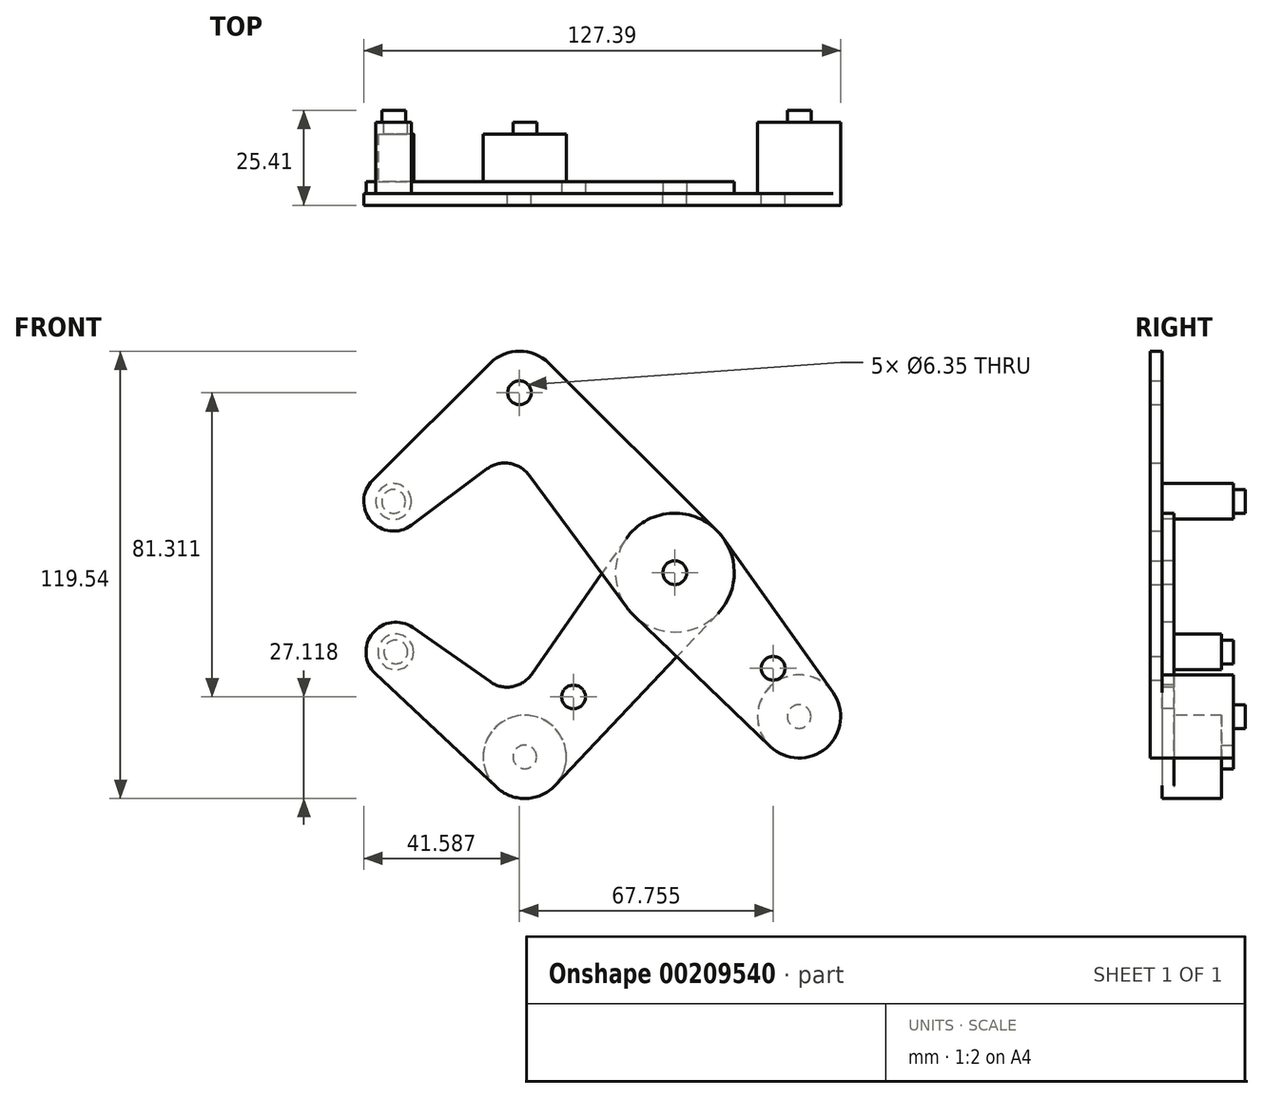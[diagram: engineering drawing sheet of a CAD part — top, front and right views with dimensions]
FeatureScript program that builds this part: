
annotation { "Feature Type Name" : "Feature", "Feature Type Description" : "" }
export const myFeature = defineFeature(function(context is Context, id is Id, definition is map)
    precondition{}
    {
        {
            var Q0;
            Q0=qCreatedBy(makeId("Front.planeOp"),FACE);
            var sketch = newSketch(context, id + "F0", { "sketchPlane" : qUnion([Q0])});
            skLineSegment(sketch, "E0", {"start": v(-41.5, 48.07) * mm, "end": v(41.5, -48.07) * mm, "construction": true});
            skCircle(sketch, "E1", {"center": v(0, 0) * mm, "radius": 3.18 * mm});
            skCircle(sketch, "E2", {"center": v(33.2, -38.45) * mm, "radius": 3.18 * mm});
            skCircle(sketch, "E3", {"center": v(-41.5, 48.07) * mm, "radius": 3.18 * mm});
            skCircle(sketch, "E4", {"center": v(-75.14, 19.02) * mm, "radius": 3.18 * mm});
            skLineSegment(sketch, "E5", {"start": v(-41.5, 48.07) * mm, "end": v(-75.14, 19.02) * mm, "construction": true});
            skCircle(sketch, "E6", {"center": v(33.2, -38.45) * mm, "radius": 11.11 * mm});
            skCircle(sketch, "E7", {"center": v(-75.14, 19.02) * mm, "radius": 7.94 * mm});
            skCircle(sketch, "E8", {"center": v(-41.5, 48.07) * mm, "radius": 11.11 * mm});
            skLineSegment(sketch, "E9", {"start": v(-80.74, 24.65) * mm, "end": v(-49.34, 55.94) * mm});
            skLineSegment(sketch, "E10", {"start": v(-70.4, 12.66) * mm, "end": v(-50.18, 27.73) * mm});
            skCircle(sketch, "E11", {"center": v(0, 0) * mm, "radius": 15.88 * mm});
            skLineSegment(sketch, "E12", {"start": v(-33.65, 55.94) * mm, "end": v(11.2, 11.25) * mm});
            skLineSegment(sketch, "E13", {"start": v(-39.05, 26.09) * mm, "end": v(-12.76, -9.44) * mm});
            skLineSegment(sketch, "E14", {"start": v(-11, -11.45) * mm, "end": v(25.5, -46.47) * mm});
            skLineSegment(sketch, "E15", {"start": v(12.94, 9.2) * mm, "end": v(42.25, -32.01) * mm});
            skArc(sketch, "E16.filletArc", {"start": v(-39.05, 26.09) * mm, "mid": v(-44.28, 29.22) * mm, "end": v(-50.18, 27.73) * mm});
            skLineSegment(sketch, "E17", {"start": v(0, 0) * mm, "end": v(-40.09, -49.25) * mm, "construction": true});
            skLineSegment(sketch, "E18", {"start": v(-40.09, -49.25) * mm, "end": v(-74.56, -21.19) * mm, "construction": true});
            skCircle(sketch, "E19", {"center": v(-74.56, -21.19) * mm, "radius": 3.18 * mm});
            skCircle(sketch, "E20", {"center": v(-40.09, -49.25) * mm, "radius": 3.18 * mm});
            skCircle(sketch, "E21", {"center": v(-74.56, -21.19) * mm, "radius": 7.94 * mm});
            skCircle(sketch, "E22", {"center": v(-40.09, -49.25) * mm, "radius": 11.11 * mm});
            skLineSegment(sketch, "E23", {"start": v(-70, -14.69) * mm, "end": v(-49.36, -29.17) * mm});
            skLineSegment(sketch, "E24", {"start": v(-80, -26.97) * mm, "end": v(-47.7, -57.34) * mm});
            skLineSegment(sketch, "E25", {"start": v(-13.03, 9.07) * mm, "end": v(-38.28, -27.2) * mm});
            skLineSegment(sketch, "E26", {"start": v(11.53, -10.92) * mm, "end": v(-32.02, -56.89) * mm});
            skArc(sketch, "E27.filletArc", {"start": v(-49.36, -29.17) * mm, "mid": v(-43.41, -30.49) * mm, "end": v(-38.28, -27.2) * mm});
            skCircle(sketch, "E28", {"center": v(-27.06, -33.24) * mm, "radius": 3.18 * mm});
            skCircle(sketch, "E29", {"center": v(26.26, -25.56) * mm, "radius": 3.18 * mm});
            skLineSegment(sketch, "E30", {"start": v(26.26, -25.56) * mm, "end": v(23.86, -27.64) * mm, "construction": true});
            skCircle(sketch, "E31", {"center": v(0, 0) * mm, "radius": 3.97 * mm});
            skSolve(sketch);
        }
        {
            var Q0;
            Q0=qCreatedBy(makeId("Front.planeOp"),FACE);
            cPlane(context, id + "F1", {"entities" : qUnion([Q0]), "cplaneType" : CPlaneType.OFFSET, "offset" : 9.52 * mm, "oppositeDirection" : true, "width" : 254 * mm, "height" : 254 * mm});
        }
        {
            var Q0;
            Q0=makeQuery(id+"F0.imprint","IMPRINT",FACE,{"disambiguationData":[TD([[makeQuery(id+"F0.imprint","IMPRINT",EDGE,{"derivedFrom":sQuery(id+"F0.wireOp",EDGE,"E4")}),-1.0]])]});
            var Q1;
            {var subQ1=sQuery(id+"F0.wireOp",EDGE,"E9");Q1=makeQuery(id+"F0.imprint","IMPRINT",FACE,{"disambiguationData":[TD([[makeQuery(id+"F0.imprint","IMPRINT",EDGE,{"derivedFrom":subQ1}),-1.0]])]});}
            var Q2;
            Q2=makeQuery(id+"F0.imprint","IMPRINT",FACE,{"disambiguationData":[TD([[makeQuery(id+"F0.imprint","IMPRINT",EDGE,{"derivedFrom":sQuery(id+"F0.wireOp",EDGE,"E3")}),-1.0]])]});
            var Q3;
            {var subQ0=sQuery(id+"F0.wireOp",EDGE,"E13");var subQ1=sQuery(id+"F0.wireOp",EDGE,"E11");var subQ2=makeQuery(id+"F0.imprint","INTERSECT",VERTEX,{"derivedFrom":[subQ1,subQ0]});Q3=makeQuery(id+"F0.imprint","IMPRINT",FACE,{"disambiguationData":[TD([[makeQuery(id+"F0.imprint","IMPRINT",EDGE,{"disambiguationData":[TD([[subQ2,1.0]])],"derivedFrom":subQ1}),-1.0]])]});}
            var Q4;
            Q4=makeQuery(id+"F0.imprint","IMPRINT",FACE,{"disambiguationData":[TD([[makeQuery(id+"F0.imprint","IMPRINT",EDGE,{"derivedFrom":sQuery(id+"F0.wireOp",EDGE,"E31")}),-1.0]])]});
            var Q5;
            {var subQ0=sQuery(id+"F0.wireOp",EDGE,"E14");var subQ1=sQuery(id+"F0.wireOp",EDGE,"E11");var subQ2=makeQuery(id+"F0.imprint","INTERSECT",VERTEX,{"derivedFrom":[subQ1,subQ0]});Q5=makeQuery(id+"F0.imprint","IMPRINT",FACE,{"disambiguationData":[TD([[makeQuery(id+"F0.imprint","IMPRINT",EDGE,{"disambiguationData":[TD([[subQ2,-1.0]])],"derivedFrom":subQ1}),-1.0]])]});}
            var Q6;
            Q6=makeQuery(id+"F0.imprint","IMPRINT",FACE,{"disambiguationData":[TD([[makeQuery(id+"F0.imprint","IMPRINT",EDGE,{"derivedFrom":sQuery(id+"F0.wireOp",EDGE,"E1")}),-1.0]])]});
            var Q7;
            {var subQ0=sQuery(id+"F0.wireOp",EDGE,"E15");Q7=makeQuery(id+"F0.imprint","IMPRINT",FACE,{"disambiguationData":[TD([[makeQuery(id+"F0.imprint","IMPRINT",EDGE,{"derivedFrom":subQ0}),-1.0]])]});}
            var Q8;
            Q8=makeQuery(id+"F0.imprint","IMPRINT",FACE,{"disambiguationData":[TD([[makeQuery(id+"F0.imprint","IMPRINT",EDGE,{"derivedFrom":sQuery(id+"F0.wireOp",EDGE,"E2")}),-1.0]])]});
            extrude(context, id + "F2", {"entities" : qUnion([Q0, Q1, Q2, Q3, Q4, Q5, Q6, Q7, Q8]), "depth" : 3.17 * mm});
        }
        {
            var Q0;
            Q0=makeQuery(id+"F0.imprint","IMPRINT",FACE,{"disambiguationData":[TD([[makeQuery(id+"F0.imprint","IMPRINT",EDGE,{"derivedFrom":sQuery(id+"F0.wireOp",EDGE,"E19")}),-1.0]])]});
            var Q1;
            {var subQ10=sQuery(id+"F0.wireOp",EDGE,"E23");Q1=makeQuery(id+"F0.imprint","IMPRINT",FACE,{"disambiguationData":[TD([[makeQuery(id+"F0.imprint","IMPRINT",EDGE,{"derivedFrom":subQ10}),-1.0]])]});}
            var Q2;
            Q2=makeQuery(id+"F0.imprint","IMPRINT",FACE,{"disambiguationData":[TD([[makeQuery(id+"F0.imprint","IMPRINT",EDGE,{"derivedFrom":sQuery(id+"F0.wireOp",EDGE,"E20")}),-1.0]])]});
            var Q3;
            {var subQ0=sQuery(id+"F0.wireOp",EDGE,"E13");var subQ1=sQuery(id+"F0.wireOp",EDGE,"E11");var subQ2=makeQuery(id+"F0.imprint","INTERSECT",VERTEX,{"derivedFrom":[subQ1,subQ0]});Q3=makeQuery(id+"F0.imprint","IMPRINT",FACE,{"disambiguationData":[TD([[makeQuery(id+"F0.imprint","IMPRINT",EDGE,{"disambiguationData":[TD([[subQ2,1.0]])],"derivedFrom":subQ1}),-1.0]])]});}
            var Q4;
            {var subQ0=sQuery(id+"F0.wireOp",EDGE,"E14");var subQ1=sQuery(id+"F0.wireOp",EDGE,"E11");var subQ2=makeQuery(id+"F0.imprint","INTERSECT",VERTEX,{"derivedFrom":[subQ1,subQ0]});Q4=makeQuery(id+"F0.imprint","IMPRINT",FACE,{"disambiguationData":[TD([[makeQuery(id+"F0.imprint","IMPRINT",EDGE,{"disambiguationData":[TD([[subQ2,-1.0]])],"derivedFrom":subQ1}),-1.0]])]});}
            var Q5;
            Q5=makeQuery(id+"F0.imprint","IMPRINT",FACE,{"disambiguationData":[TD([[makeQuery(id+"F0.imprint","IMPRINT",EDGE,{"derivedFrom":sQuery(id+"F0.wireOp",EDGE,"E31")}),-1.0]])]});
            var Q6;
            Q6=makeQuery(id+"F0.imprint","IMPRINT",FACE,{"disambiguationData":[TD([[makeQuery(id+"F0.imprint","IMPRINT",EDGE,{"derivedFrom":sQuery(id+"F0.wireOp",EDGE,"E1")}),-1.0]])]});
            extrude(context, id + "F3", {"entities" : qUnion([Q0, Q1, Q2, Q3, Q4, Q5, Q6]), "oppositeDirection" : true, "depth" : 3.17 * mm});
        }
        {
            var Q0;
            Q0=makeQuery(id+"F2.opExtrude","CAP_FACE",FACE,{"disambiguationData":[OSD([sQuery(id+"F0.wireOp",EDGE,"E1"),sQuery(id+"F0.wireOp",EDGE,"E2"),sQuery(id+"F0.wireOp",EDGE,"E3"),sQuery(id+"F0.wireOp",EDGE,"E4"),sQuery(id+"F0.wireOp",EDGE,"E6"),sQuery(id+"F0.wireOp",EDGE,"E7"),sQuery(id+"F0.wireOp",EDGE,"E8"),sQuery(id+"F0.wireOp",EDGE,"E9"),sQuery(id+"F0.wireOp",EDGE,"E10"),sQuery(id+"F0.wireOp",EDGE,"E11"),sQuery(id+"F0.wireOp",EDGE,"E12"),sQuery(id+"F0.wireOp",EDGE,"E13"),sQuery(id+"F0.wireOp",EDGE,"E14"),sQuery(id+"F0.wireOp",EDGE,"E15"),sQuery(id+"F0.wireOp",EDGE,"E16.filletArc"),sQuery(id+"F0.wireOp",EDGE,"E29")])],"isStart":false});
            var sketch = newSketch(context, id + "F4", { "sketchPlane" : qUnion([Q0])});
            skCircle(sketch, "E32", {"center": v(-75.14, 19.02) * mm, "radius": 4.76 * mm});
            skCircle(sketch, "E33", {"center": v(33.2, -38.45) * mm, "radius": 11.11 * mm});
            skSolve(sketch);
        }
        {
            var Q0;
            {var subQ10=sQuery(id+"F0.wireOp",EDGE,"E23");Q0=makeQuery(id+"F0.imprint","IMPRINT",FACE,{"disambiguationData":[TD([[makeQuery(id+"F0.imprint","IMPRINT",EDGE,{"derivedFrom":subQ10}),-1.0]])]});}
            var sketch = newSketch(context, id + "F5", { "sketchPlane" : qUnion([Q0])});
            skCircle(sketch, "E34", {"center": v(-74.56, -21.19) * mm, "radius": 4.76 * mm});
            skCircle(sketch, "E35", {"center": v(-40.09, -49.25) * mm, "radius": 11.11 * mm});
            skSolve(sketch);
        }
        {
            var Q0;
            Q0=qSketchRegion(id+"F5",true);
            var Q1;
            Q1=qSketchRegion(id+"F4",true);
            var Q2;
            Q2=qCreatedBy(id+"F1.planeOp",FACE);
            extrude(context, id + "F6", {"entities" : qUnion([Q0, Q1]), "endBound" : BoundingType.UP_TO_SURFACE, "oppositeDirection" : true, "endBoundEntityFace" : qUnion([Q2]), "depth" : 25.4 * mm});
        }
        {
            var Q0;
            Q0=makeQuery(id+"F2.opExtrude","SWEPT_BODY",BODY,{"disambiguationData":[OSD([sQuery(id+"F0.wireOp",EDGE,"E1"),sQuery(id+"F0.wireOp",EDGE,"E2"),sQuery(id+"F0.wireOp",EDGE,"E3"),sQuery(id+"F0.wireOp",EDGE,"E4"),sQuery(id+"F0.wireOp",EDGE,"E6"),sQuery(id+"F0.wireOp",EDGE,"E7"),sQuery(id+"F0.wireOp",EDGE,"E8"),sQuery(id+"F0.wireOp",EDGE,"E9"),sQuery(id+"F0.wireOp",EDGE,"E10"),sQuery(id+"F0.wireOp",EDGE,"E11"),sQuery(id+"F0.wireOp",EDGE,"E12"),sQuery(id+"F0.wireOp",EDGE,"E13"),sQuery(id+"F0.wireOp",EDGE,"E14"),sQuery(id+"F0.wireOp",EDGE,"E15"),sQuery(id+"F0.wireOp",EDGE,"E16.filletArc"),sQuery(id+"F0.wireOp",EDGE,"E29")])]});
            var Q1;
            Q1=makeQuery(id+"F3.opExtrude","SWEPT_BODY",BODY,{"disambiguationData":[OSD([sQuery(id+"F0.wireOp",EDGE,"E1"),sQuery(id+"F0.wireOp",EDGE,"E11"),sQuery(id+"F0.wireOp",EDGE,"E19"),sQuery(id+"F0.wireOp",EDGE,"E20"),sQuery(id+"F0.wireOp",EDGE,"E21"),sQuery(id+"F0.wireOp",EDGE,"E22"),sQuery(id+"F0.wireOp",EDGE,"E23"),sQuery(id+"F0.wireOp",EDGE,"E24"),sQuery(id+"F0.wireOp",EDGE,"E25"),sQuery(id+"F0.wireOp",EDGE,"E26"),sQuery(id+"F0.wireOp",EDGE,"E27.filletArc"),sQuery(id+"F0.wireOp",EDGE,"E28")])]});
            var Q2;
            Q2=makeQuery(id+"F6.opExtrude","SWEPT_BODY",BODY,{"disambiguationData":[OSD([sQuery(id+"F4.wireOp",EDGE,"E33")])]});
            var Q3;
            Q3=makeQuery(id+"F6.opExtrude","SWEPT_BODY",BODY,{"disambiguationData":[OSD([sQuery(id+"F5.wireOp",EDGE,"E35")])]});
            var Q4;
            Q4=makeQuery(id+"F6.opExtrude","SWEPT_BODY",BODY,{"disambiguationData":[OSD([sQuery(id+"F5.wireOp",EDGE,"E34")])]});
            var Q5;
            Q5=makeQuery(id+"F6.opExtrude","SWEPT_BODY",BODY,{"disambiguationData":[OSD([sQuery(id+"F4.wireOp",EDGE,"E32")])]});
            booleanBodies(context, id + "F7", {"operationType" : BooleanOperationType.SUBTRACTION, "tools" : qUnion([Q0, Q1]), "targets" : qUnion([Q2, Q3, Q4, Q5]), "keepTools" : true});
        }
        {
            var Q0;
            Q0=makeQuery(id+"F6.opExtrude","SWEPT_BODY",BODY,{"disambiguationData":[OSD([sQuery(id+"F4.wireOp",EDGE,"E33")])]});
            var Q1;
            Q1=makeQuery(id+"F6.opExtrude","SWEPT_BODY",BODY,{"disambiguationData":[OSD([sQuery(id+"F5.wireOp",EDGE,"E35")])]});
            var Q2;
            Q2=makeQuery(id+"F6.opExtrude","SWEPT_BODY",BODY,{"disambiguationData":[OSD([sQuery(id+"F4.wireOp",EDGE,"E32")])]});
            var Q3;
            Q3=makeQuery(id+"F6.opExtrude","SWEPT_BODY",BODY,{"disambiguationData":[OSD([sQuery(id+"F5.wireOp",EDGE,"E34")])]});
            var Q4;
            Q4=qCreatedBy(id+"F1.planeOp",FACE);
            mirror(context, id + "F8", {"operationType" : NewBodyOperationType.ADD, "entities" : qUnion([Q0, Q1, Q2, Q3]), "mirrorPlane" : qUnion([Q4])});
        }
    });
